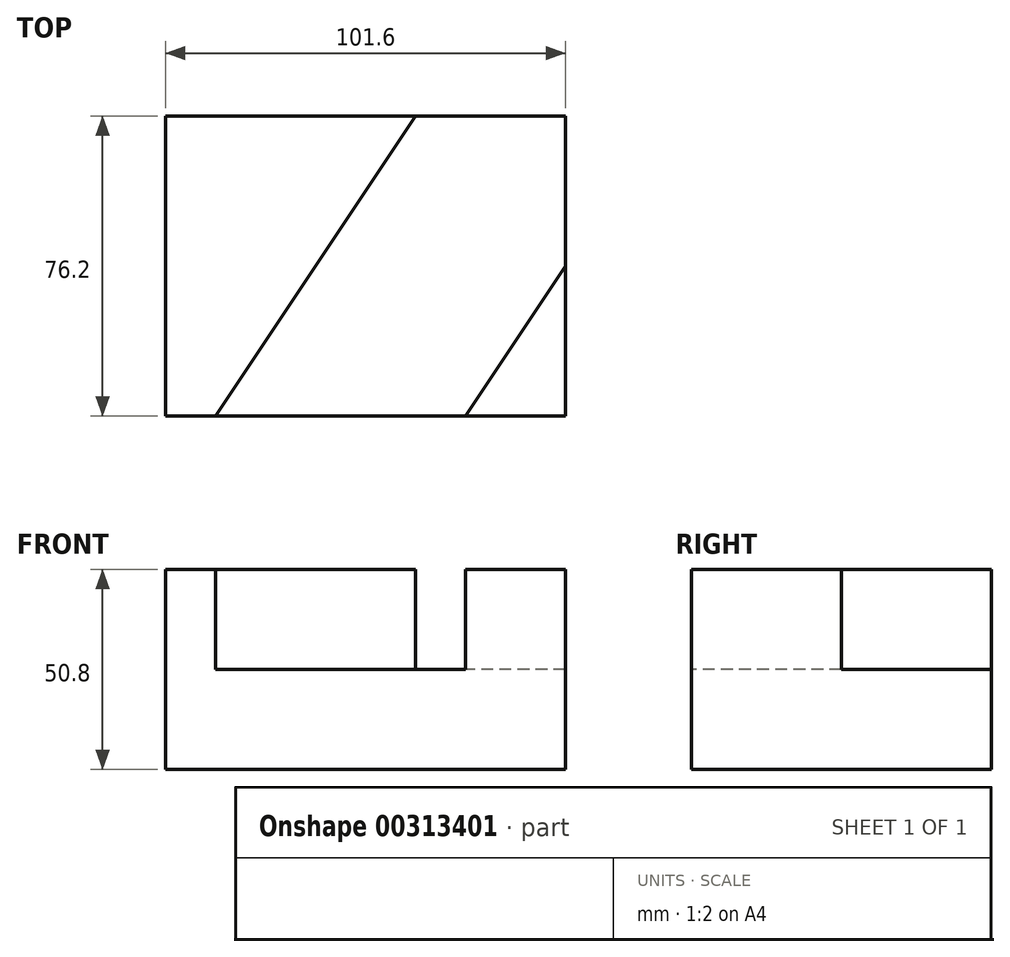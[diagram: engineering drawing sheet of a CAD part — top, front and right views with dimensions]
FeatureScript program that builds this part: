
annotation { "Feature Type Name" : "Feature", "Feature Type Description" : "" }
export const myFeature = defineFeature(function(context is Context, id is Id, definition is map)
    precondition{}
    {
        {
            var Q0;
            Q0=qCreatedBy(makeId("Top.planeOp"),FACE);
            var sketch = newSketch(context, id + "F0", { "sketchPlane" : qUnion([Q0])});
            skLineSegment(sketch, "E0", {"start": v(-40.73, -52.33) * mm, "end": v(60.87, -52.33) * mm});
            skLineSegment(sketch, "E1", {"start": v(60.87, -52.33) * mm, "end": v(60.87, 23.87) * mm});
            skLineSegment(sketch, "E2", {"start": v(60.87, 23.87) * mm, "end": v(-40.73, 23.87) * mm});
            skLineSegment(sketch, "E3", {"start": v(-40.73, 23.87) * mm, "end": v(-40.73, -52.33) * mm});
            skSolve(sketch);
        }
        {
            var Q0;
            Q0=makeQuery(id+"F0.imprint","IMPRINT",FACE,{"disambiguationData":[TD([[makeQuery(id+"F0.imprint","IMPRINT",EDGE,{"derivedFrom":sQuery(id+"F0.wireOp",EDGE,"E0")}),1.0]])]});
            extrude(context, id + "F1", {"entities" : qUnion([Q0]), "depth" : 50.8 * mm});
        }
        {
            var Q0;
            Q0=makeQuery(id+"F1.opExtrude","CAP_FACE",FACE,{"disambiguationData":[OSD([sQuery(id+"F0.wireOp",EDGE,"E0"),sQuery(id+"F0.wireOp",EDGE,"E1"),sQuery(id+"F0.wireOp",EDGE,"E2"),sQuery(id+"F0.wireOp",EDGE,"E3")])],"isStart":false});
            var sketch = newSketch(context, id + "F2", { "sketchPlane" : qUnion([Q0])});
            skLineSegment(sketch, "E4", {"start": v(60.87, -52.33) * mm, "end": v(35.47, -52.33) * mm});
            skLineSegment(sketch, "E5", {"start": v(60.87, -52.33) * mm, "end": v(60.87, -14.23) * mm});
            skLineSegment(sketch, "E6", {"start": v(60.87, -14.23) * mm, "end": v(35.47, -52.33) * mm});
            skSolve(sketch);
        }
        {
            var Q0;
            {var subQ2=sQuery(id+"F2.wireOp",EDGE,"E6");Q0=makeQuery(id+"F2.imprint","IMPRINT",FACE,{"disambiguationData":[TD([[makeQuery(id+"F2.imprint","IMPRINT",EDGE,{"derivedFrom":subQ2}),-1.0]])]});}
            extrude(context, id + "F3", {"entities" : qUnion([Q0]), "operationType" : NewBodyOperationType.REMOVE, "oppositeDirection" : true, "depth" : 25.4 * mm});
        }
        {
            var Q0;
            Q0=makeQuery(id+"F3.boolean.opBoolean","COPY",FACE,{"derivedFrom":makeQuery(id+"F3.opExtrude","CAP_FACE",FACE,{"disambiguationData":[OSD([sQuery(id+"F0.wireOp",EDGE,"E0"),sQuery(id+"F0.wireOp",EDGE,"E1"),sQuery(id+"F0.wireOp",EDGE,"E2"),sQuery(id+"F0.wireOp",EDGE,"E3"),sQuery(id+"F2.wireOp",EDGE,"E6")])],"isStart":false})});
            var sketch = newSketch(context, id + "F4", { "sketchPlane" : qUnion([Q0])});
            skLineSegment(sketch, "E7", {"start": v(-40.73, -52.33) * mm, "end": v(-28.03, -52.33) * mm});
            skLineSegment(sketch, "E8", {"start": v(-40.73, 23.87) * mm, "end": v(22.77, 23.87) * mm});
            skLineSegment(sketch, "E9", {"start": v(-40.73, 23.87) * mm, "end": v(-40.73, -52.33) * mm});
            skLineSegment(sketch, "E10", {"start": v(22.77, 23.87) * mm, "end": v(-28.03, -52.33) * mm});
            skSolve(sketch);
        }
        {
            var Q0;
            Q0=makeQuery(id+"F4.imprint","IMPRINT",FACE,{"disambiguationData":[TD([[makeQuery(id+"F4.imprint","IMPRINT",EDGE,{"derivedFrom":sQuery(id+"F4.wireOp",EDGE,"E7")}),1.0]])]});
            extrude(context, id + "F5", {"entities" : qUnion([Q0]), "operationType" : NewBodyOperationType.ADD, "depth" : 25.4 * mm});
        }
    });
